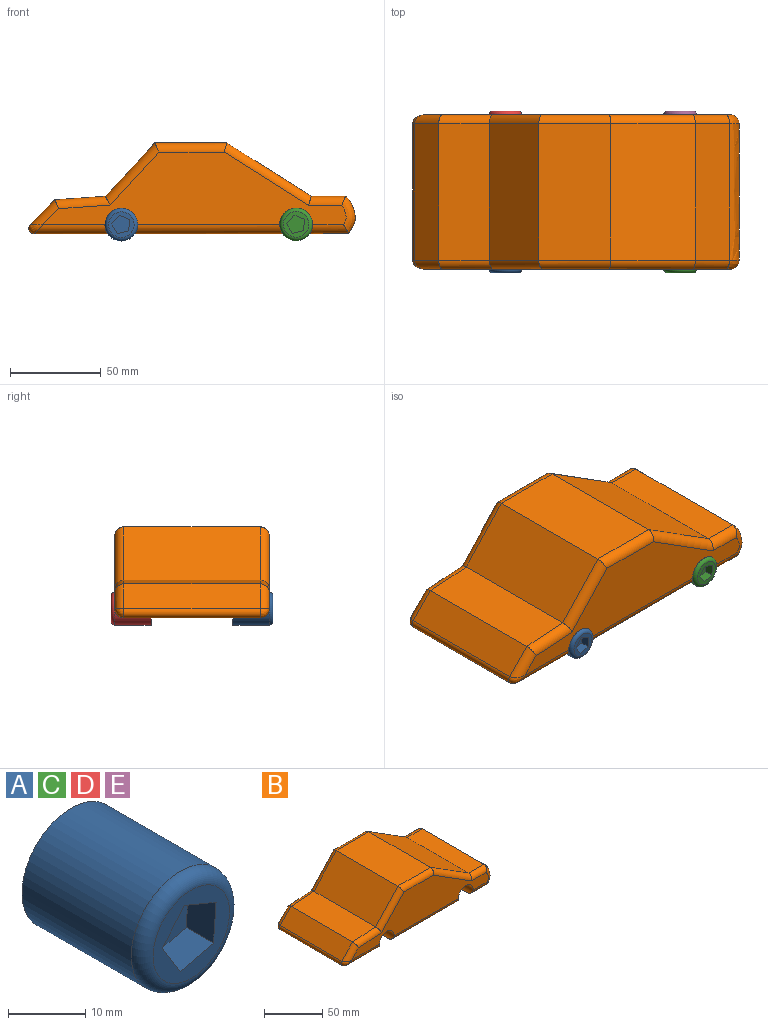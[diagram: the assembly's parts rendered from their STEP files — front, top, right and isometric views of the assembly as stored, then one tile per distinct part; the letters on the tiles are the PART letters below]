
ASSEMBLY  parts=5 mates=4
PART A: 10 faces, bbox 19.5x22x19.5 mm
  f0: cylinder r=9mm len=20mm, axis (0,1,0), area 1131mm2, adj f2,f3
  f1: plane 14x14mm, normal (0,-1,0), area 86.4mm2, adj f3,f4,f5,f6,f7,f8
  f2: plane 18x18mm, normal (0,1,0), area 254.5mm2, adj f0
  f3: torus R=7mm, axis (0,-1,0), area 163.3mm2, adj f0,f1
  f4: plane 6.25x5mm, normal (-1,0,0.08), area 31.3mm2, adj f1,f5,f8,f9
  f5: plane 5.79x5mm, normal (-0.38,0,-0.92), area 31.3mm2, adj f1,f4,f6,f9
  f6: plane 5x4.77mm, normal (0.76,0,-0.65), area 31.3mm2, adj f1,f5,f7,f9
  f7: plane 5.34x5mm, normal (0.85,0,0.52), area 31.3mm2, adj f1,f6,f8,f9
  f8: plane 6.09x5mm, normal (-0.24,0,0.97), area 31.3mm2, adj f1,f4,f7,f9
  f9: plane 10.11x9.85mm, normal (0,-1,0), area 67.5mm2, adj f4,f5,f6,f7,f8
PART B: 41 faces, bbox 183.6x85.4x51.4 mm
  f0: plane 172.85x75mm, normal (0,0,-1), area 12065.4mm2, adj f2,f3,f4,f5,f6,f11,f15,f23
  f1: plane 166.65x39.99mm, normal (0,1,0), area 3553.7mm2, adj f2,f3,f4,f29,f30,f31,f32,f33
  f2: cylinder r=5mm len=81.16mm, axis (1,0,0), area 625.5mm2, adj f0,f1,f37,f39
  f3: cylinder r=5mm len=21.39mm, axis (1,0,0), area 150.7mm2, adj f0,f1,f32,f39
  f4: cylinder r=5mm len=40.38mm, axis (1,0,0), area 292.4mm2, adj f0,f1,f35,f37
  f5: cylinder r=5mm len=81.16mm, axis (-1,0,0), area 625.5mm2, adj f0,f14,f25,f27
  f6: cylinder r=5mm len=40.38mm, axis (-1,0,0), area 292.4mm2, adj f0,f14,f24,f25
  f7: plane 75x39.61mm, normal (0,0,1), area 2970.9mm2, adj f8,f13,f16,f31
  f8: plane 75x29.32mm, normal (-0.73,0,0.68), area 2997mm2, adj f7,f9,f18,f33
  f9: plane 75x27.92mm, normal (-0.07,0,1), area 2099.2mm2, adj f8,f10,f20,f34
  f10: plane 75x13.61mm, normal (-0.71,0,0.7), area 1429.4mm2, adj f9,f15,f22,f36
  f11: extruded ~75x20.46mm, area 1715.2mm2, adj f0,f12,f21,f32
  f12: plane 75x18.71mm, normal (0,0,1), area 1403.1mm2, adj f11,f13,f19,f30
  f13: plane 75x46.39mm, normal (0.53,0,0.85), area 4116.1mm2, adj f7,f12,f17,f29
  f14: plane 166.64x39.99mm, normal (0,-1,0), area 3553.7mm2, adj f5,f6,f16,f17,f18,f19,f20,f21
  f15: cylinder r=3mm len=75mm, axis (0,-1,0), area 528.2mm2, adj f0,f10,f24,f35
  f16: cylinder r=5mm len=39.61mm, axis (1,0,0), area 296.9mm2, adj f7,f14,f17,f18
  f17: cylinder r=5mm len=50.29mm, axis (0.85,0,-0.53), area 431mm2, adj f13,f14,f16,f19
  f18: cylinder r=5mm len=34.17mm, axis (0.68,0,0.73), area 313mm2, adj f8,f14,f16,f20
  f19: cylinder r=5mm len=20.16mm, axis (1,0,0), area 144.8mm2, adj f12,f14,f17,f21
  f20: cylinder r=5mm len=30.25mm, axis (1,0,0.07), area 220.1mm2, adj f9,f14,f18,f22
  f21: bspline ~22.13x8.85mm, area 138.2mm2, adj f11,f14,f19,f23
  f22: cylinder r=5mm len=17.11mm, axis (0.7,0,0.71), area 123.5mm2, adj f10,f14,f20,f24
  f23: cylinder r=5mm len=21.39mm, axis (-1,0,0), area 150.7mm2, adj f0,f14,f21,f27
  f24: bspline ~11.92x5.93mm, area 28.8mm2, adj f6,f15,f22
  f25: cylinder r=9mm len=20mm, axis (0,-1,0), area 751mm2, adj f0,f5,f6,f14,f26
  f26: plane 18x14.01mm, normal (0,-1,0), area 212.4mm2, adj f0,f25
  f27: cylinder r=9mm len=20mm, axis (0,-1,0), area 751mm2, adj f0,f5,f14,f23,f28
  f28: plane 18x14.01mm, normal (0,-1,0), area 212.4mm2, adj f0,f27
  f29: cylinder r=5mm len=50.29mm, axis (-0.85,0,0.53), area 431mm2, adj f1,f13,f30,f31
  f30: cylinder r=5mm len=20.16mm, axis (-1,0,0), area 144.8mm2, adj f1,f12,f29,f32
  f31: cylinder r=5mm len=39.61mm, axis (-1,0,0), area 296.9mm2, adj f1,f7,f29,f33
  f32: bspline ~22.13x8.86mm, area 138.2mm2, adj f1,f3,f11,f30
  f33: cylinder r=5mm len=34.17mm, axis (-0.68,0,-0.73), area 313mm2, adj f1,f8,f31,f34
  f34: cylinder r=5mm len=30.25mm, axis (-1,0,-0.07), area 220.1mm2, adj f1,f9,f33,f36
  f35: bspline ~11.92x5.93mm, area 29.5mm2, adj f4,f15,f36
  f36: cylinder r=5mm len=17.11mm, axis (-0.7,0,-0.71), area 123.5mm2, adj f1,f10,f34,f35
  f37: cylinder r=9mm len=20mm, axis (0,1,0), area 751mm2, adj f0,f1,f2,f4,f38
  f38: plane 18x14.01mm, normal (0,1,0), area 212.4mm2, adj f0,f37
  f39: cylinder r=9mm len=20mm, axis (0,1,0), area 751mm2, adj f0,f1,f2,f3,f40
  f40: plane 18x14.01mm, normal (0,1,0), area 212.4mm2, adj f0,f39
PART C: same geometry as A
PART D: same geometry as A
PART E: same geometry as A
PLACE A t=(-50.54,-30.54,-22.15)mm
PLACE B t=(-14.6,34.46,-6.54)mm fixed
PLACE C t=(45.58,-30.54,-22.03)mm
PLACE D rot(axis=(0,0,1),180deg) t=(-50.54,14.46,-22.15)mm
PLACE E rot(axis=(0,0,1),180deg) t=(45.58,14.46,-22.03)mm
MATE revolute C.f0 <-> B.f27  axis (0,1,0) through (45.58,-30.54,-22.03)mm
MATE revolute E.f0 <-> B.f27  axis (0,-1,0) through (45.58,14.46,-22.03)mm
MATE revolute D.f0 <-> B.f25  axis (0,-1,0) through (-50.54,14.46,-22.15)mm
MATE revolute A.f0 <-> B.f25  axis (0,1,0) through (-50.54,-30.54,-22.15)mm
